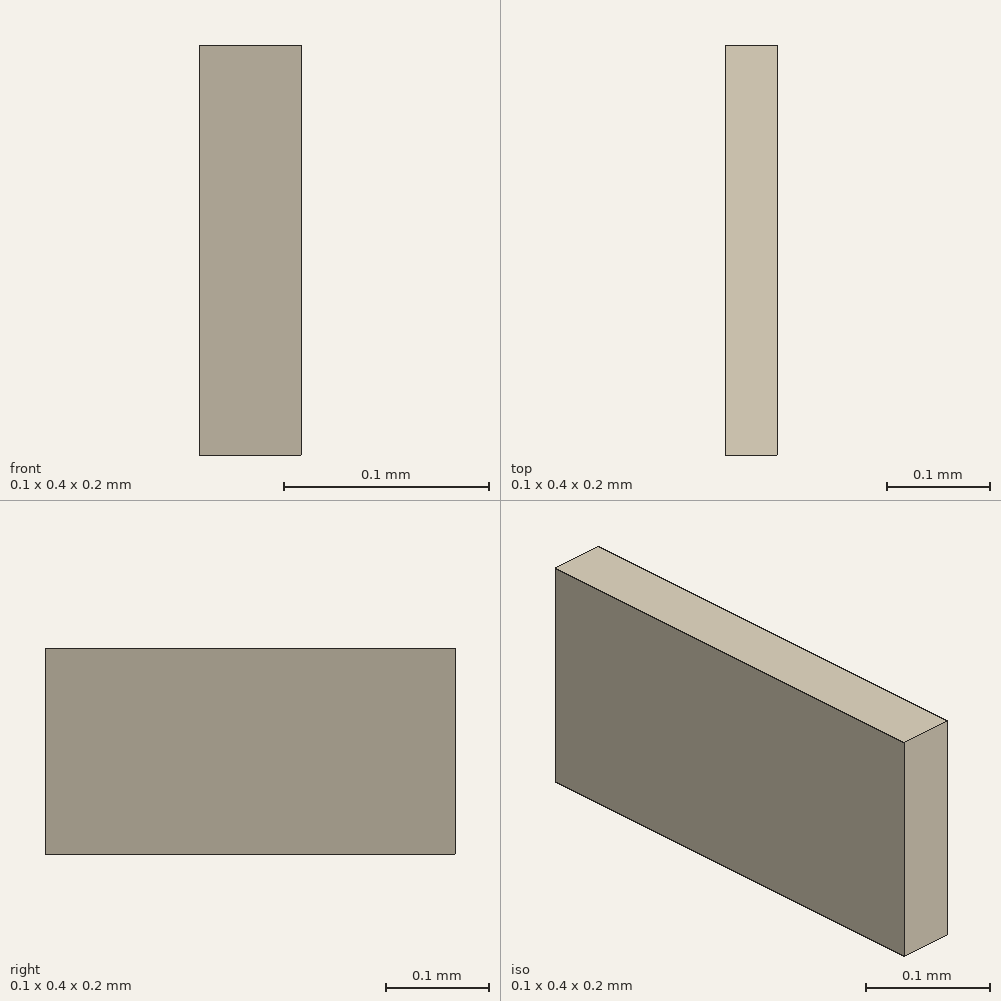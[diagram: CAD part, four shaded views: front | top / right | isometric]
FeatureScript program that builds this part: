
annotation { "Feature Type Name" : "Feature", "Feature Type Description" : "" }
export const myFeature = defineFeature(function(context is Context, id is Id, definition is map)
    precondition{}
    {
        {
            var Q0;
            Q0=qCreatedBy(makeId("Right.planeOp"),FACE);
            var sketch = newSketch(context, id + "F0", { "sketchPlane" : qUnion([Q0])});
            skLineSegment(sketch, "E0.bottom", {"start": v(-0.2, -0.1) * mm, "end": v(0.2, -0.1) * mm});
            skLineSegment(sketch, "E0.top", {"start": v(-0.2, 0.1) * mm, "end": v(0.2, 0.1) * mm});
            skLineSegment(sketch, "E0.left", {"start": v(-0.2, -0.1) * mm, "end": v(-0.2, 0.1) * mm});
            skLineSegment(sketch, "E0.right", {"start": v(0.2, -0.1) * mm, "end": v(0.2, 0.1) * mm});
            skSolve(sketch);
        }
        {
            var Q0;
            Q0=makeQuery(id+"F0.imprint","IMPRINT",FACE,{"disambiguationData":[TD([[makeQuery(id+"F0.imprint","IMPRINT",EDGE,{"derivedFrom":sQuery(id+"F0.wireOp",EDGE,"E0.bottom")}),1.0]])]});
            extrude(context, id + "F1", {"entities" : qUnion([Q0]), "depth" : 0.03 * mm, "hasSecondDirection" : true, "secondDirectionOppositeDirection" : true, "secondDirectionDepth" : 0.03 * mm});
        }
    });
